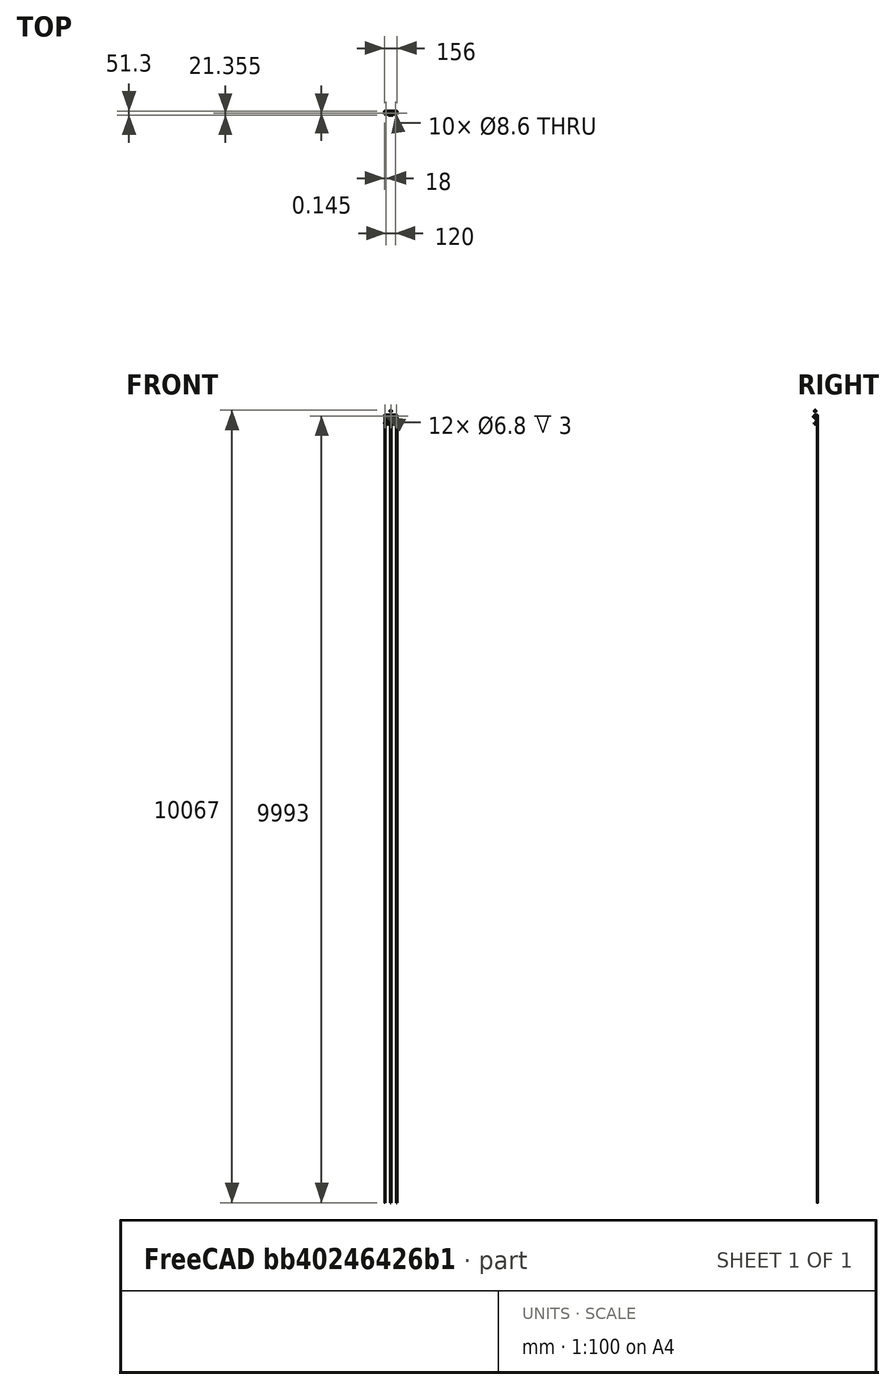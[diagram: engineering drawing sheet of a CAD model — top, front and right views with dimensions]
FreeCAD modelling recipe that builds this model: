
FCSTD DOCUMENT  (FreeCAD 0.15R4671 (Git))
Label: ZRodHolderBottom
License: All rights reserved
LicenseURL: http://en.wikipedia.org/wiki/All_rights_reserved
objects: Sketcher::SketchObject×7, PartDesign::Fillet×6, PartDesign::Pocket×5, Part::Feature×3, PartDesign::Pad×2, PartDesign::Chamfer×1, Mesh::Feature×1
note: 31 computed .brp shape members not serialized (recipe doc carries the construction recipe); baked Part::Feature solids carry a one-line shape summary decoded from their .brp

FEATURE [Part::Feature] Part__Feature  label="TempZMotorEnd"
  shape: bbox 155 x 49.5 x 115 mm, 106 faces (baked)
FEATURE [Part::Feature] _mmBrasNut  label="8mmBrassNut"
  Placement = pos=(0,-28.14,59) rot=(0.707107,0,0.707107;3.14159rad)
  shape: bbox 22 x 22 x 16.42 mm, 29 faces (baked)
FEATURE [Sketcher::SketchObject] Sketch
  Placement = pos=(0,0,0) rot=(1,0,0;1.5708rad)
  sketch-geometry (4):
    g0: LineSegment StartX=-78 StartY=7.5 StartZ=0 EndX=78 EndY=7.5 EndZ=0
    g1: LineSegment StartX=78 StartY=7.5 StartZ=0 EndX=78 EndY=-7.5 EndZ=0
    g2: LineSegment StartX=78 StartY=-7.5 StartZ=0 EndX=-78 EndY=-7.5 EndZ=0
    g3: LineSegment StartX=-78 StartY=-7.5 StartZ=0 EndX=-78 EndY=7.5 EndZ=0
  constraints (12):
    c: Coincident(g0,g1)
    c: Coincident(g1,g2)
    c: Coincident(g2,g3)
    c: Coincident(g3,g0)
    c: Horizontal(g0)
    c: Horizontal(g2)
    c: Vertical(g1)
    c: Vertical(g3)
    c: DistanceY(g1,g0) = 15
    c: DistanceY(g-1,g1) = -7.5
    c: DistanceX(g1,g2) = -156
    c: DistanceX(g-1,g2) = -78
FEATURE [PartDesign::Pad] Pad
  Length = 36
  Length2 = 100
  Placement = pos=(0,0,0) rot=(1,0,0;1.5708rad)
  Sketch = -> Sketch
  Type = 0
FEATURE [Sketcher::SketchObject] Sketch001
  Placement = pos=(0,0,7.5) rot=(0,0,1;3.14159rad)
  Support = -> Pad [Face1]
  sketch-geometry (16):
    g0: LineSegment StartX=-80 StartY=7 StartZ=0 EndX=-68 EndY=7 EndZ=0
    g1: LineSegment StartX=-68 StartY=7 StartZ=0 EndX=-68 EndY=37 EndZ=0
    g2: LineSegment StartX=-68 StartY=37 StartZ=0 EndX=-52 EndY=37 EndZ=0
    g3: LineSegment StartX=-52 StartY=37 StartZ=0 EndX=-52 EndY=28 EndZ=0
    g4: LineSegment StartX=-52 StartY=28 StartZ=0 EndX=-32 EndY=7 EndZ=0
    g5: LineSegment StartX=-32 StartY=7 StartZ=0 EndX=32 EndY=7 EndZ=0
    g6: LineSegment StartX=32 StartY=7 StartZ=0 EndX=52 EndY=28 EndZ=0
    g7: LineSegment StartX=52 StartY=28 StartZ=0 EndX=52 EndY=37 EndZ=0
    g8: LineSegment StartX=52 StartY=37 StartZ=0 EndX=68 EndY=37 EndZ=0
    g9: LineSegment StartX=68 StartY=37 StartZ=0 EndX=68 EndY=7 EndZ=0
    g10: LineSegment StartX=68 StartY=7 StartZ=0 EndX=80 EndY=7 EndZ=0
    g11: LineSegment StartX=80 StartY=7 StartZ=0 EndX=80 EndY=53.5948 EndZ=0
    g12: LineSegment StartX=80 StartY=53.5948 StartZ=0 EndX=-80 EndY=53.5948 EndZ=0
    g13: LineSegment StartX=-80 StartY=53.5948 StartZ=0 EndX=-80 EndY=7 EndZ=0
    g14: Circle CenterX=-60 CenterY=28 CenterZ=0 NormalX=0 NormalY=0 NormalZ=1 Radius=4.3
    g15: Circle CenterX=60 CenterY=28 CenterZ=0 NormalX=0 NormalY=0 NormalZ=1 Radius=4.3
  constraints (27):
    c: Coincident(g0,g1)
    c: Coincident(g1,g2)
    c: Coincident(g2,g3)
    c: Coincident(g3,g4)
    c: Coincident(g4,g5)
    c: Coincident(g5,g6)
    c: Coincident(g6,g7)
    c: Coincident(g7,g8)
    c: Coincident(g8,g9)
    c: Coincident(g9,g10)
    c: Coincident(g10,g11)
    c: Coincident(g11,g12)
    c: Coincident(g12,g13)
    c: Coincident(g13,g0)
    c: Horizontal(g12)
    c: Vertical(g11)
    c: Vertical(g13)
    c: Vertical(g9)
    c: Vertical(g7)
    c: Vertical(g3)
    c: Vertical(g1)
    c: Horizontal(g2)
    c: Horizontal(g8)
    c: Horizontal(g10)
    c: Horizontal(g0)
    c: Radius(g15) = 4.3
    c: Equal(g15,g14)
FEATURE [PartDesign::Pocket] Pocket
  Length = 5
  Placement = pos=(0,0,0) rot=(1,0,0;1.5708rad)
  Sketch = -> Sketch001
  Type = 1
FEATURE [PartDesign::Chamfer] Chamfer
  Base = -> Pocket [Edge24,Edge27,Edge36,Edge39]
  Placement = pos=(0,0,0) rot=(1,0,0;1.5708rad)
  Size = 4
FEATURE [PartDesign::Fillet] Fillet
  Base = -> Chamfer [Edge21,Edge24,Edge28,Edge33,Edge52,Edge54,Edge51,Edge46]
  Placement = pos=(0,0,0) rot=(1,0,0;1.5708rad)
  Radius = 2
FEATURE [PartDesign::Fillet] Fillet001
  Base = -> Fillet [Edge72,Edge68,Edge64,Edge60,Edge30,Edge51]
  Placement = pos=(0,0,0) rot=(1,0,0;1.5708rad)
  Radius = 2
FEATURE [Sketcher::SketchObject] Sketch002
  Placement = pos=(0,-7,0) rot=(1,0,0;1.5708rad)
  Support = -> Fillet001 [Face26]
  sketch-geometry (3):
    g0: Circle CenterX=0 CenterY=0 CenterZ=0 NormalX=0 NormalY=0 NormalZ=1 Radius=1.8
    g1: Circle CenterX=74 CenterY=0 CenterZ=0 NormalX=0 NormalY=0 NormalZ=1 Radius=1.8
    g2: Circle CenterX=-74 CenterY=0 CenterZ=0 NormalX=0 NormalY=0 NormalZ=1 Radius=1.8
  constraints (3):
    c: Radius(g2) = 1.8
    c: Equal(g2,g0)
    c: Equal(g2,g1)
FEATURE [PartDesign::Pocket] Pocket001
  Length = 5
  Placement = pos=(0,0,0) rot=(1,0,0;1.5708rad)
  Sketch = -> Sketch002
  Type = 1
FEATURE [Sketcher::SketchObject] Sketch003
  Placement = pos=(0,-7,0) rot=(1,0,0;1.5708rad)
  Support = -> Pocket001 [Face26]
  sketch-geometry (3):
    g0: Circle CenterX=0 CenterY=0 CenterZ=0 NormalX=0 NormalY=0 NormalZ=1 Radius=3.4
    g1: Circle CenterX=74 CenterY=0 CenterZ=0 NormalX=0 NormalY=0 NormalZ=1 Radius=3.4
    g2: Circle CenterX=-74 CenterY=0 CenterZ=0 NormalX=0 NormalY=0 NormalZ=1 Radius=3.4
  constraints (3):
    c: Radius(g2) = 3.4
    c: Equal(g2,g0)
    c: Equal(g2,g1)
FEATURE [PartDesign::Pocket] Pocket002
  Length = 3
  Placement = pos=(0,0,0) rot=(1,0,0;1.5708rad)
  Sketch = -> Sketch003
  Type = 0
FEATURE [PartDesign::Fillet] Fillet002
  Base = -> Pocket002 [Edge59,Edge10,Edge48,Edge6]
  Placement = pos=(0,0,0) rot=(1,0,0;1.5708rad)
  Radius = 4
FEATURE [Mesh::Feature] MicroSwitch
  Placement = pos=(68.3,-20,3) rot=(0.57735,0.57735,0.57735;2.0944rad)
FEATURE [Sketcher::SketchObject] Sketch004
  Placement = pos=(68,0,0) rot=(0.707107,0,0.707107;3.14159rad)
  Support = -> Fillet002 [Face6]
  sketch-geometry (2):
    g0: Circle CenterX=0.25 CenterY=24.5 CenterZ=0 NormalX=0 NormalY=0 NormalZ=1 Radius=1
    g1: Circle CenterX=0.25 CenterY=15 CenterZ=0 NormalX=0 NormalY=0 NormalZ=1 Radius=1
  constraints (2):
    c: Radius(g1) = 1
    c: Equal(g1,g0)
FEATURE [PartDesign::Pocket] Pocket003  label="ZRodHolderMiddle_1"
  Length = 4
  Placement = pos=(0,0,0) rot=(1,0,0;1.5708rad)
  Sketch = -> Sketch004
  Type = 0
FEATURE [PartDesign::Fillet] Fillet003
  Base = -> Pocket003 [Edge26]
  Placement = pos=(0,0,0) rot=(1,0,0;1.5708rad)
  Radius = 1
FEATURE [Part::Feature] Fillet004  label="ZRodHolderMiddle_2"
  shape: bbox 156.7 x 36 x 15.66 mm, 122 faces (baked)
FEATURE [Sketcher::SketchObject] Sketch005
  Placement = pos=(0,0,7.5) rot=(0,0,1;0rad)
  Support = -> Fillet004 [Face1]
  sketch-geometry (8):
    g0: LineSegment StartX=65 StartY=-6 StartZ=0 EndX=36 EndY=-6 EndZ=0
    g1: LineSegment StartX=36 StartY=-6 StartZ=0 EndX=51 EndY=-21 EndZ=0
    g2: LineSegment StartX=51 StartY=-21 StartZ=0 EndX=65 EndY=-21 EndZ=0
    g3: LineSegment StartX=65 StartY=-21 StartZ=0 EndX=65 EndY=-6 EndZ=0
    g4: LineSegment StartX=-37 StartY=-7 StartZ=0 EndX=-65 EndY=-7 EndZ=0
    g5: LineSegment StartX=-65 StartY=-7 StartZ=0 EndX=-65 EndY=-21 EndZ=0
    g6: LineSegment StartX=-65 StartY=-21 StartZ=0 EndX=-51 EndY=-21 EndZ=0
    g7: LineSegment StartX=-51 StartY=-21 StartZ=0 EndX=-37 EndY=-7 EndZ=0
  constraints (8):
    c: Coincident(g0,g1)
    c: Coincident(g1,g2)
    c: Coincident(g2,g3)
    c: Coincident(g3,g0)
    c: Coincident(g4,g5)
    c: Coincident(g5,g6)
    c: Coincident(g6,g7)
    c: Coincident(g7,g4)
FEATURE [PartDesign::Pocket] Pocket004
  Length = 12
  Sketch = -> Sketch005
  Type = 0
FEATURE [PartDesign::Fillet] Fillet005
  Base = -> Pocket004 [Edge128,Edge134,Edge132,Edge130,Edge118,Edge120,Edge122,Edge124]
  Radius = 2
FEATURE [PartDesign::Fillet] Fillet006  label="ZRodHolderMiddle"
  Base = -> Fillet005 [Edge6,Edge45]
  Radius = 1
FEATURE [Sketcher::SketchObject] Sketch006
  Placement = pos=(0,0,-7.5) rot=(1,0,0;3.14159rad)
  Support = -> Fillet006 [Face66]
  sketch-geometry (2):
    g0: Circle CenterX=-60 CenterY=28 CenterZ=0 NormalX=0 NormalY=0 NormalZ=1 Radius=6
    g1: Circle CenterX=60 CenterY=28 CenterZ=0 NormalX=0 NormalY=0 NormalZ=1 Radius=6
FEATURE [PartDesign::Pad] Pad001  label="ZRodHolderBottom"
  Length = 5
  Length2 = 100
  Reversed = true
  Sketch = -> Sketch006
  Type = 0
